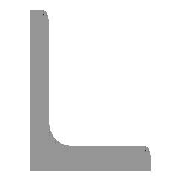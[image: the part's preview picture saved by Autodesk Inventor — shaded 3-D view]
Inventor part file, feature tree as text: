
AUTODESK INVENTOR PART (.ipt)
format: ipt  version: 2022 (Build 260153000, 153)  size: 163,328 bytes
history: native  units: mm (DEFAULTED — no unit token found)
features: other x5, sketch x2, sweep x1, plane x1
ambient origin geometry x8: Origin, YZ Plane, XZ Plane, XY Plane, X Axis, Y Axis, Z Axis, Center Point
bodies: Solid1 (feature_tree), Body (feature_tree)
feature tree (9):
  parser-record x1  (decoder bookkeeping rows leaked as tree rows — omitted from the tree; the rows remain in map.json)
  other  "Driven Length"
  other  "Start plane"
  other  "End plane"
  sweep  "Sweep Path"
  other  "Orientation Work Plane"
  sketch  "Sketch3"  dims[d3=50.0mm d4=60.0mm]
  plane  "Work Plane10"
  sketch  "Sketch4"  dims[d5=50.0mm d6=60.0mm d7=4.0mm d8=8.0mm d9=4.0mm d10=8.0mm d17=8.0mm d18=4.0mm d19=17.7mm d20=17.7mm d21=-0.0mm d22=2815.406592mm d23=90.0deg d24=2815.406592mm d25=0.0mm d26=0.0mm]
